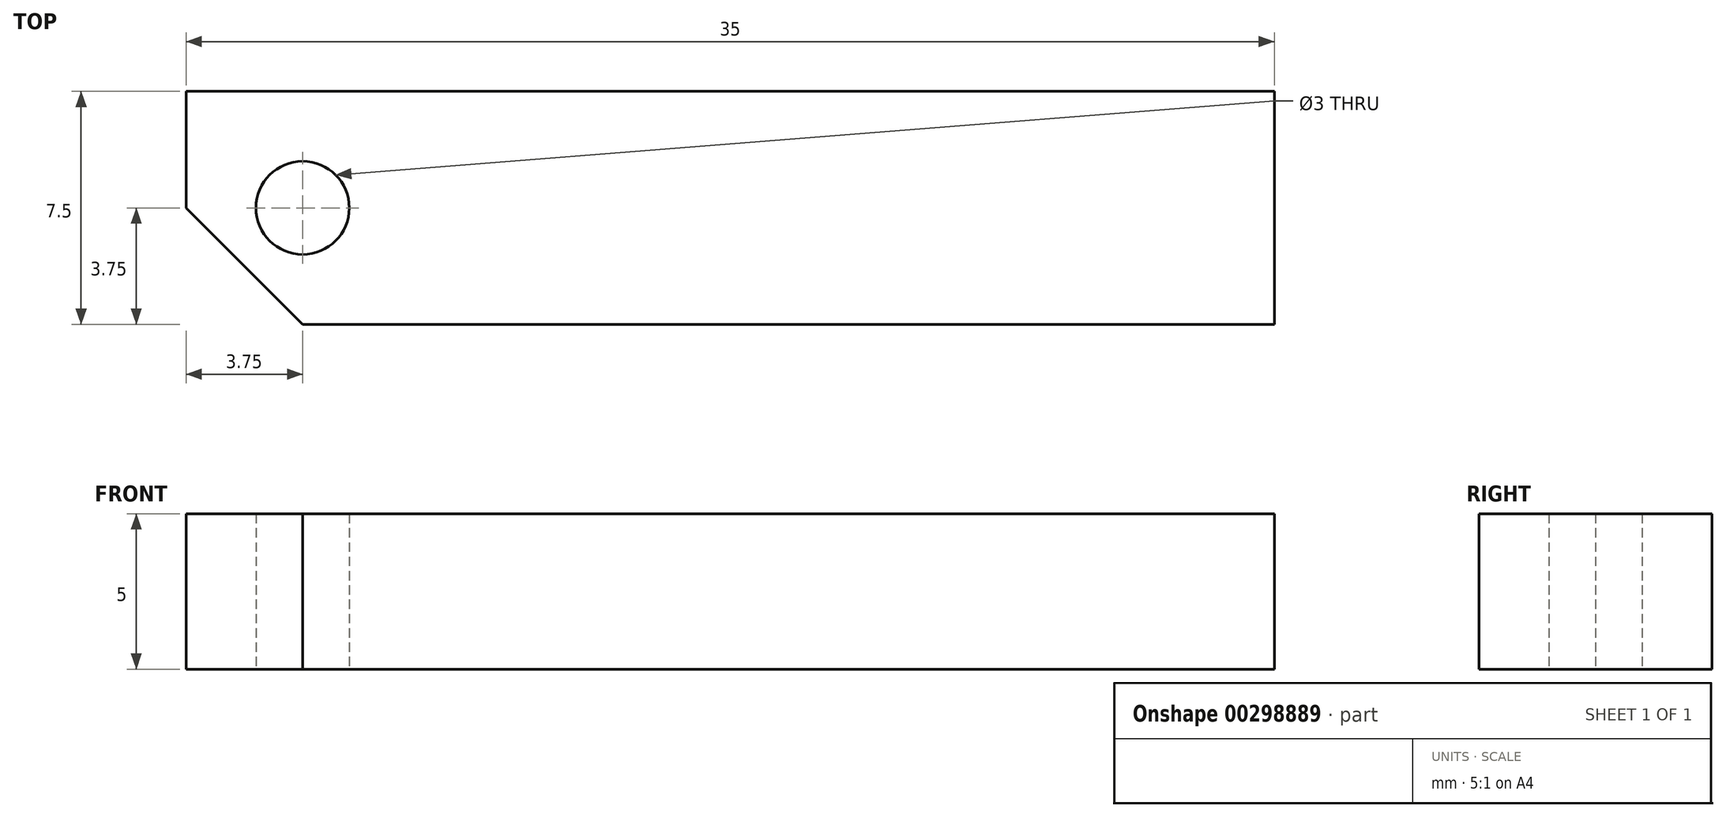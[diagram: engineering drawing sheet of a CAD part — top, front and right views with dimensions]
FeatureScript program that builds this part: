
annotation { "Feature Type Name" : "Feature", "Feature Type Description" : "" }
export const myFeature = defineFeature(function(context is Context, id is Id, definition is map)
    precondition{}
    {
        {
            var Q0;
            Q0=qCreatedBy(makeId("Top.planeOp"),FACE);
            var sketch = newSketch(context, id + "F0", { "sketchPlane" : qUnion([Q0])});
            skLineSegment(sketch, "E0.top", {"start": v(7.5, 15) * mm, "end": v(-7.5, 15) * mm});
            skLineSegment(sketch, "E0.left", {"start": v(7.5, -7.5) * mm, "end": v(7.5, 15) * mm});
            skLineSegment(sketch, "E0.right", {"start": v(-7.5, -3.75) * mm, "end": v(-7.5, 15) * mm});
            skPoint(sketch, "E0.middle", {"position": v(0, 0) * mm});
            skLineSegment(sketch, "E1", {"start": v(-3.75, -7.5) * mm, "end": v(0, -7.5) * mm});
            skLineSegment(sketch, "E2.bottom", {"start": v(0, -7.5) * mm, "end": v(-3.75, -7.5) * mm});
            skLineSegment(sketch, "E2.right", {"start": v(-7.5, -3.75) * mm, "end": v(-7.5, 0) * mm});
            skPoint(sketch, "E3.centerSnap0", {"position": v(-7.5, -3.75) * mm});
            skPoint(sketch, "E3.centerSnap1", {"position": v(-3.75, 0) * mm});
            skCircle(sketch, "E4", {"center": v(-3.75, -3.75) * mm, "radius": 1.5 * mm});
            skLineSegment(sketch, "E5", {"start": v(7.5, -7.5) * mm, "end": v(0, -7.5) * mm});
            skLineSegment(sketch, "E6", {"start": v(-3.75, -7.5) * mm, "end": v(-3.75, -11.25) * mm});
            skArc(sketch, "E7", {"start": v(-6.4, -13.9) * mm, "mid": v(-0.29, -12.69) * mm, "end": v(-3.75, -7.5) * mm});
            skLineSegment(sketch, "E8", {"start": v(-3.75, -11.25) * mm, "end": v(-6.4, -13.9) * mm});
            skLineSegment(sketch, "E9", {"start": v(-6.4, -13.9) * mm, "end": v(-3.75, -11.25) * mm});
            skLineSegment(sketch, "E10", {"start": v(-6.4, -13.9) * mm, "end": v(-6.4, -16.4) * mm});
            skLineSegment(sketch, "E11", {"start": v(-6.4, -16.4) * mm, "end": v(0, -16.4) * mm});
            skLineSegment(sketch, "E12", {"start": v(-7.5, -3.75) * mm, "end": v(-3.75, -7.5) * mm});
            skLineSegment(sketch, "E13", {"start": v(7.5, -7.5) * mm, "end": v(7.5, -16.4) * mm});
            skLineSegment(sketch, "E14", {"start": v(7.5, -16.4) * mm, "end": v(0, -16.4) * mm});
            skSolve(sketch);
        }
        {
            var Q0;
            Q0=makeQuery(id+"F0.imprint","IMPRINT",FACE,{"disambiguationData":[TD([[makeQuery(id+"F0.imprint","IMPRINT",EDGE,{"derivedFrom":sQuery(id+"F0.wireOp",EDGE,"E0.top")}),1.0]])]});
            var Q1;
            Q1=makeQuery(id+"F0.imprint","IMPRINT",FACE,{"disambiguationData":[TD([[makeQuery(id+"F0.imprint","IMPRINT",EDGE,{"derivedFrom":sQuery(id+"F0.wireOp",EDGE,"E2.bottom")}),1.0]])]});
            extrude(context, id + "F1", {"entities" : qUnion([Q0, Q1]), "depth" : 5 * mm});
        }
        {
            var Q0;
            Q0=makeQuery(id+"F1.opExtrude","CAP_FACE",FACE,{"disambiguationData":[OSD([sQuery(id+"F0.wireOp",EDGE,"E0.top"),sQuery(id+"F0.wireOp",EDGE,"E0.left"),sQuery(id+"F0.wireOp",EDGE,"E0.right"),sQuery(id+"F0.wireOp",EDGE,"E2.right"),sQuery(id+"F0.wireOp",EDGE,"E4"),sQuery(id+"F0.wireOp",EDGE,"E7"),sQuery(id+"F0.wireOp",EDGE,"E10"),sQuery(id+"F0.wireOp",EDGE,"E11"),sQuery(id+"F0.wireOp",EDGE,"8CcDkt48-7C2M-Xkuw-v35Y-0lNiqKwsLmXV"),sQuery(id+"F0.wireOp",EDGE,"E12")])],"isStart":false});
            var sketch = newSketch(context, id + "F2", { "sketchPlane" : qUnion([Q0])});
            skLineSegment(sketch, "E15.bottom", {"start": v(-7.5, 15) * mm, "end": v(7.5, 15) * mm});
            skLineSegment(sketch, "E15.top", {"start": v(-7.5, 0) * mm, "end": v(7.5, 0) * mm});
            skLineSegment(sketch, "E15.left", {"start": v(-7.5, 15) * mm, "end": v(-7.5, 0) * mm});
            skLineSegment(sketch, "E15.right", {"start": v(7.5, 15) * mm, "end": v(7.5, 0) * mm});
            skSolve(sketch);
        }
        {
            var Q0;
            Q0 = qSketchRegion(id + "F2", true);
            extrude(context, id + "F3", {"entities" : qUnion([Q0]), "operationType" : NewBodyOperationType.REMOVE, "oppositeDirection" : true, "depth" : 25 * mm});
        }
        {
            var Q0;
            Q0=makeQuery(id+"F1.opExtrude","SWEPT_FACE",FACE,{"disambiguationData":[OSD([sQuery(id+"F0.wireOp",EDGE,"E0.left"),sQuery(id+"F0.wireOp",EDGE,"E13")])]});
            extrude(context, id + "F4", {"entities" : qUnion([Q0]), "operationType" : NewBodyOperationType.ADD, "depth" : 20 * mm});
        }
    });
